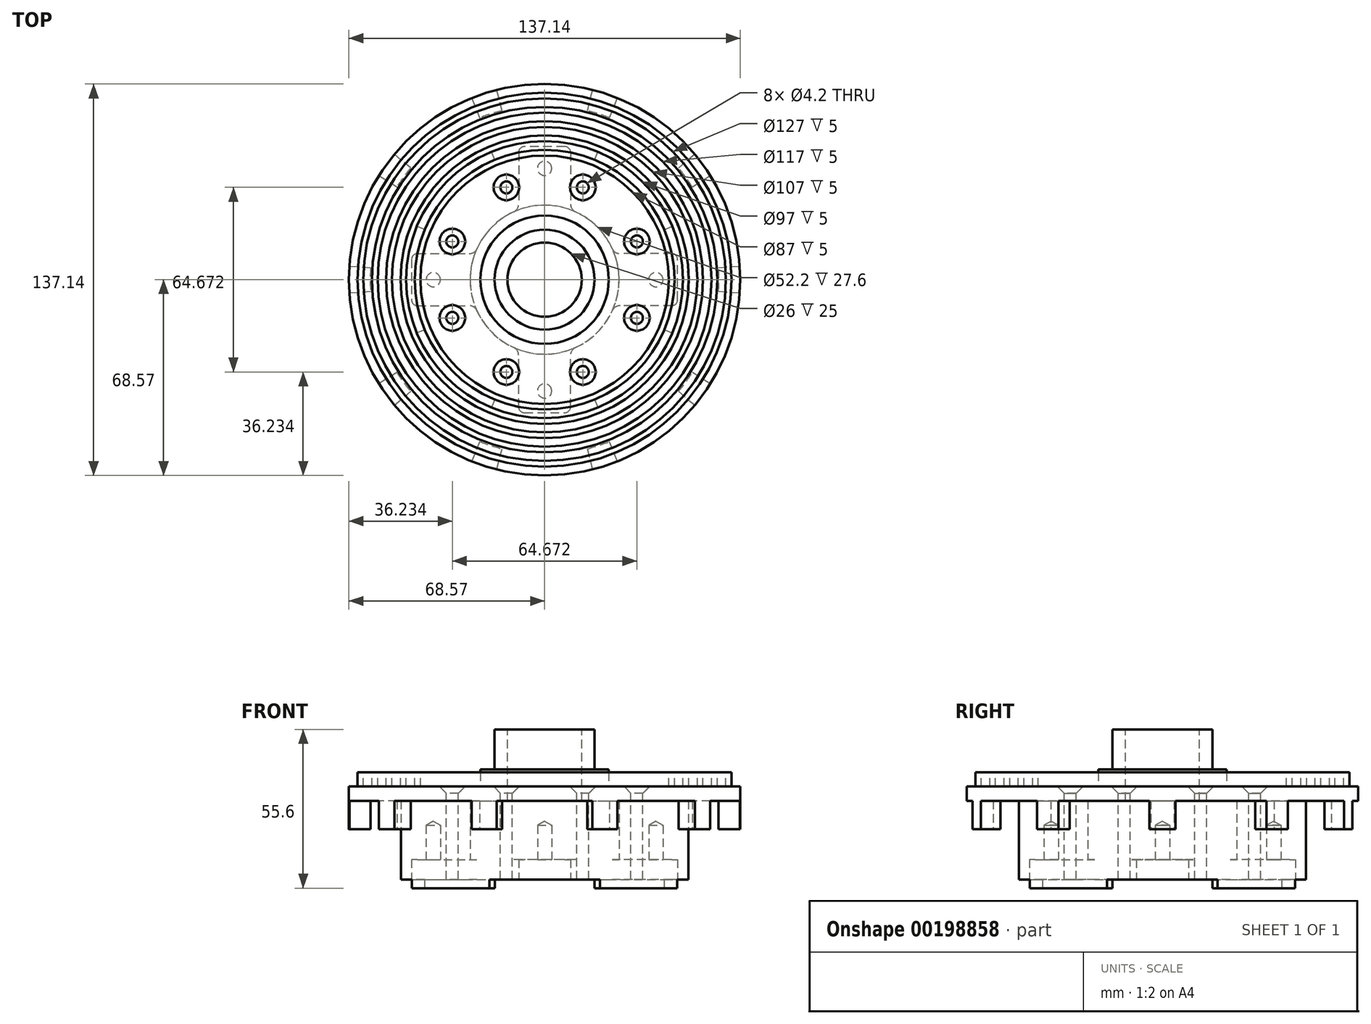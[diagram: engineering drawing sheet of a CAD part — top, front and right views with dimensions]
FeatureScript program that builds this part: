
annotation { "Feature Type Name" : "Feature", "Feature Type Description" : "" }
export const myFeature = defineFeature(function(context is Context, id is Id, definition is map)
    precondition{}
    {
        {
            var Q0;
            Q0=qCreatedBy(makeId("Top.planeOp"),FACE);
            var sketch = newSketch(context, id + "F0", { "sketchPlane" : qUnion([Q0])});
            skCircle(sketch, "E0", {"center": v(0, 0) * mm, "radius": 50.15 * mm, "construction": true});
            skCircle(sketch, "E1", {"center": v(0, 0) * mm, "radius": 68.57 * mm});
            skCircle(sketch, "E2", {"center": v(0, 0) * mm, "radius": 61.01 * mm, "construction": true});
            skSolve(sketch);
        }
        {
            var Q0;
            Q0 = qSketchRegion(id + "F0", true);
            extrude(context, id + "F1", {"entities" : qUnion([Q0]), "depth" : 27.6 * mm});
        }
        {
            var Q0;
            Q0=makeQuery(id+"F1.opExtrude","CAP_FACE",FACE,{"disambiguationData":[OSD([sQuery(id+"F0.wireOp",EDGE,"E1")])],"isStart":true});
            var sketch = newSketch(context, id + "F2", { "sketchPlane" : qUnion([Q0])});
            skLineSegment(sketch, "E3", {"start": v(0, 0) * mm, "end": v(-16.76, -66.49) * mm, "construction": true});
            skLineSegment(sketch, "E4", {"start": v(0, 0) * mm, "end": v(20.02, -79.4) * mm, "construction": true});
            skLineSegment(sketch, "E5", {"start": v(-14.91, -59.15) * mm, "end": v(14.91, -59.15) * mm});
            skLineSegment(sketch, "E6", {"start": v(-14.91, -59.15) * mm, "end": v(-18.58, -73.7) * mm});
            skLineSegment(sketch, "E7", {"start": v(-18.58, -73.7) * mm, "end": v(18.58, -73.7) * mm});
            skLineSegment(sketch, "E8", {"start": v(18.58, -73.7) * mm, "end": v(14.91, -59.15) * mm});
            skSolve(sketch);
        }
        {
            var Q0;
            Q0 = qSketchRegion(id + "F2", true);
            extrude(context, id + "F3", {"entities" : qUnion([Q0]), "endBound" : BoundingType.SYMMETRIC, "depth" : 75 * mm});
        }
        {
            var Q0;
            Q0=makeQuery(id+"F3.opExtrude","SWEPT_BODY",BODY,{"disambiguationData":[OSD([sQuery(id+"F2.wireOp",EDGE,"E5"),sQuery(id+"F2.wireOp",EDGE,"E6"),sQuery(id+"F2.wireOp",EDGE,"E7"),sQuery(id+"F2.wireOp",EDGE,"E8")])]});
            var Q1;
            Q1=makeQuery(id+"F1.opExtrude","SWEPT_FACE",FACE,{"disambiguationData":[OSD([sQuery(id+"F0.wireOp",EDGE,"E1")])]});
            circularPattern(context, id + "F4", {"entities" : qUnion([Q0]), "axis" : qUnion([Q1]), "angle" : 36 * degree, "instanceCount" : 10});
        }
        {
            var Q0;
            Q0=makeQuery(id+"F4.opPattern","COPY",BODY,{"derivedFrom":makeQuery(id+"F3.opExtrude","SWEPT_BODY",BODY,{"disambiguationData":[OSD([sQuery(id+"F2.wireOp",EDGE,"E5"),sQuery(id+"F2.wireOp",EDGE,"E6"),sQuery(id+"F2.wireOp",EDGE,"E7"),sQuery(id+"F2.wireOp",EDGE,"E8")])]}),"instanceName":"7"});
            var Q1;
            Q1=makeQuery(id+"F4.opPattern","COPY",BODY,{"derivedFrom":makeQuery(id+"F3.opExtrude","SWEPT_BODY",BODY,{"disambiguationData":[OSD([sQuery(id+"F2.wireOp",EDGE,"E5"),sQuery(id+"F2.wireOp",EDGE,"E6"),sQuery(id+"F2.wireOp",EDGE,"E7"),sQuery(id+"F2.wireOp",EDGE,"E8")])]}),"instanceName":"8"});
            var Q2;
            Q2=makeQuery(id+"F4.opPattern","COPY",BODY,{"derivedFrom":makeQuery(id+"F3.opExtrude","SWEPT_BODY",BODY,{"disambiguationData":[OSD([sQuery(id+"F2.wireOp",EDGE,"E5"),sQuery(id+"F2.wireOp",EDGE,"E6"),sQuery(id+"F2.wireOp",EDGE,"E7"),sQuery(id+"F2.wireOp",EDGE,"E8")])]}),"instanceName":"9"});
            var Q3;
            Q3=makeQuery(id+"F3.opExtrude","SWEPT_BODY",BODY,{"disambiguationData":[OSD([sQuery(id+"F2.wireOp",EDGE,"E5"),sQuery(id+"F2.wireOp",EDGE,"E6"),sQuery(id+"F2.wireOp",EDGE,"E7"),sQuery(id+"F2.wireOp",EDGE,"E8")])]});
            var Q4;
            Q4=makeQuery(id+"F4.opPattern","COPY",BODY,{"derivedFrom":makeQuery(id+"F3.opExtrude","SWEPT_BODY",BODY,{"disambiguationData":[OSD([sQuery(id+"F2.wireOp",EDGE,"E5"),sQuery(id+"F2.wireOp",EDGE,"E6"),sQuery(id+"F2.wireOp",EDGE,"E7"),sQuery(id+"F2.wireOp",EDGE,"E8")])]}),"instanceName":"1"});
            var Q5;
            Q5=makeQuery(id+"F4.opPattern","COPY",BODY,{"derivedFrom":makeQuery(id+"F3.opExtrude","SWEPT_BODY",BODY,{"disambiguationData":[OSD([sQuery(id+"F2.wireOp",EDGE,"E5"),sQuery(id+"F2.wireOp",EDGE,"E6"),sQuery(id+"F2.wireOp",EDGE,"E7"),sQuery(id+"F2.wireOp",EDGE,"E8")])]}),"instanceName":"2"});
            var Q6;
            Q6=makeQuery(id+"F4.opPattern","COPY",BODY,{"derivedFrom":makeQuery(id+"F3.opExtrude","SWEPT_BODY",BODY,{"disambiguationData":[OSD([sQuery(id+"F2.wireOp",EDGE,"E5"),sQuery(id+"F2.wireOp",EDGE,"E6"),sQuery(id+"F2.wireOp",EDGE,"E7"),sQuery(id+"F2.wireOp",EDGE,"E8")])]}),"instanceName":"3"});
            var Q7;
            Q7=makeQuery(id+"F4.opPattern","COPY",BODY,{"derivedFrom":makeQuery(id+"F3.opExtrude","SWEPT_BODY",BODY,{"disambiguationData":[OSD([sQuery(id+"F2.wireOp",EDGE,"E5"),sQuery(id+"F2.wireOp",EDGE,"E6"),sQuery(id+"F2.wireOp",EDGE,"E7"),sQuery(id+"F2.wireOp",EDGE,"E8")])]}),"instanceName":"4"});
            var Q8;
            Q8=makeQuery(id+"F4.opPattern","COPY",BODY,{"derivedFrom":makeQuery(id+"F3.opExtrude","SWEPT_BODY",BODY,{"disambiguationData":[OSD([sQuery(id+"F2.wireOp",EDGE,"E5"),sQuery(id+"F2.wireOp",EDGE,"E6"),sQuery(id+"F2.wireOp",EDGE,"E7"),sQuery(id+"F2.wireOp",EDGE,"E8")])]}),"instanceName":"5"});
            var Q9;
            Q9=makeQuery(id+"F4.opPattern","COPY",BODY,{"derivedFrom":makeQuery(id+"F3.opExtrude","SWEPT_BODY",BODY,{"disambiguationData":[OSD([sQuery(id+"F2.wireOp",EDGE,"E5"),sQuery(id+"F2.wireOp",EDGE,"E6"),sQuery(id+"F2.wireOp",EDGE,"E7"),sQuery(id+"F2.wireOp",EDGE,"E8")])]}),"instanceName":"6"});
            var Q10;
            Q10=makeQuery(id+"F1.opExtrude","SWEPT_BODY",BODY,{"disambiguationData":[OSD([sQuery(id+"F0.wireOp",EDGE,"E1")])]});
            booleanBodies(context, id + "F5", {"operationType" : BooleanOperationType.SUBTRACTION, "tools" : qUnion([Q0, Q1, Q2, Q3, Q4, Q5, Q6, Q7, Q8, Q9]), "targets" : qUnion([Q10])});
        }
        {
            var Q0;
            Q0=makeQuery(id+"F1.opExtrude","CAP_FACE",FACE,{"disambiguationData":[OSD([sQuery(id+"F0.wireOp",EDGE,"E1")])],"isStart":false});
            var sketch = newSketch(context, id + "F6", { "sketchPlane" : qUnion([Q0])});
            skCircle(sketch, "E9", {"center": v(0, 0) * mm, "radius": 68.57 * mm});
            skSolve(sketch);
        }
        {
            var Q0;
            Q0 = qSketchRegion(id + "F6", true);
            extrude(context, id + "F7", {"entities" : qUnion([Q0]), "operationType" : NewBodyOperationType.ADD, "depth" : 10 * mm});
        }
        {
            var Q0;
            Q0=makeQuery(id+"F1.opExtrude","CAP_FACE",FACE,{"disambiguationData":[OSD([sQuery(id+"F0.wireOp",EDGE,"E1")])],"isStart":true});
            var sketch = newSketch(context, id + "F8", { "sketchPlane" : qUnion([Q0])});
            skCircle(sketch, "E10", {"center": v(0, 0) * mm, "radius": 50.35 * mm});
            skCircle(sketch, "E11", {"center": v(0, 0) * mm, "radius": 61.1 * mm});
            skSolve(sketch);
        }
        {
            var Q0;
            Q0 = qSketchRegion(id + "F8", true);
            extrude(context, id + "F9", {"entities" : qUnion([Q0]), "operationType" : NewBodyOperationType.REMOVE, "oppositeDirection" : true, "depth" : 27.6 * mm});
        }
        {
            var Q0;
            Q0=qCreatedBy(makeId("Front.planeOp"),FACE);
            var sketch = newSketch(context, id + "F10", { "sketchPlane" : qUnion([Q0])});
            skLineSegment(sketch, "E12", {"start": v(0, 42.6) * mm, "end": v(-100, 42.6) * mm});
            skLineSegment(sketch, "E13", {"start": v(-100, 42.6) * mm, "end": v(-100, 32.6) * mm});
            skLineSegment(sketch, "E14", {"start": v(-100, 32.6) * mm, "end": v(-65.5, 32.6) * mm});
            skLineSegment(sketch, "E15", {"start": v(-65.5, 32.6) * mm, "end": v(-65.5, 39.6) * mm});
            skLineSegment(sketch, "E16", {"start": v(-65.5, 39.6) * mm, "end": v(-63.5, 39.6) * mm});
            skLineSegment(sketch, "E17", {"start": v(-63.5, 39.6) * mm, "end": v(-63.5, 32.6) * mm});
            skLineSegment(sketch, "E18", {"start": v(-63.5, 32.6) * mm, "end": v(-60.5, 32.6) * mm});
            skLineSegment(sketch, "E19", {"start": v(-60.5, 32.6) * mm, "end": v(-60.5, 39.6) * mm});
            skLineSegment(sketch, "E20", {"start": v(-60.5, 39.6) * mm, "end": v(-58.5, 39.6) * mm});
            skLineSegment(sketch, "E21", {"start": v(-58.5, 39.6) * mm, "end": v(-58.5, 32.6) * mm});
            skLineSegment(sketch, "E22", {"start": v(-58.5, 32.6) * mm, "end": v(-55.5, 32.6) * mm});
            skLineSegment(sketch, "E23", {"start": v(-55.5, 32.6) * mm, "end": v(-55.5, 39.6) * mm});
            skLineSegment(sketch, "E24", {"start": v(-55.5, 39.6) * mm, "end": v(-53.5, 39.6) * mm});
            skLineSegment(sketch, "E25", {"start": v(-53.5, 39.6) * mm, "end": v(-53.5, 32.6) * mm});
            skLineSegment(sketch, "E26", {"start": v(-53.5, 32.6) * mm, "end": v(-50.5, 32.6) * mm});
            skLineSegment(sketch, "E27", {"start": v(-50.5, 32.6) * mm, "end": v(-50.5, 39.6) * mm});
            skLineSegment(sketch, "E28", {"start": v(-50.5, 39.6) * mm, "end": v(-48.5, 39.6) * mm});
            skLineSegment(sketch, "E29", {"start": v(-48.5, 39.6) * mm, "end": v(-48.5, 32.6) * mm});
            skLineSegment(sketch, "E30", {"start": v(-48.5, 32.6) * mm, "end": v(-45.5, 32.6) * mm});
            skLineSegment(sketch, "E31", {"start": v(-45.5, 32.6) * mm, "end": v(-45.5, 39.6) * mm});
            skLineSegment(sketch, "E32", {"start": v(-45.5, 39.6) * mm, "end": v(-43.5, 39.6) * mm});
            skLineSegment(sketch, "E33", {"start": v(-43.5, 39.6) * mm, "end": v(-43.5, 32.6) * mm});
            skLineSegment(sketch, "E34", {"start": v(-43.5, 32.6) * mm, "end": v(0, 32.6) * mm});
            skLineSegment(sketch, "E35", {"start": v(0, 32.6) * mm, "end": v(0, 42.6) * mm});
            skSolve(sketch);
        }
        {
            var Q0;
            Q0 = qSketchRegion(id + "F10", true);
            var Q1;
            Q1=sQuery(id+"F10.wireOp",EDGE,"E35");
            revolve(context, id + "F11", {"operationType" : NewBodyOperationType.REMOVE, "entities" : qUnion([Q0]), "axis" : qUnion([Q1]), "revolveType" : RevolveType.FULL, "oppositeDirection" : true});
        }
        {
            var Q0;
            Q0=makeQuery(id+"F11.boolean.opBoolean","COPY",FACE,{"derivedFrom":makeQuery(id+"F11.opRevolve","SWEPT_FACE",FACE,{"disambiguationData":[OSD([sQuery(id+"F10.wireOp",EDGE,"E34")])]})});
            var sketch = newSketch(context, id + "F12", { "sketchPlane" : qUnion([Q0])});
            skCircle(sketch, "E36", {"center": v(0, 0) * mm, "radius": 22.5 * mm});
            skSolve(sketch);
        }
        {
            var Q0;
            Q0 = qSketchRegion(id + "F12", true);
            extrude(context, id + "F13", {"entities" : qUnion([Q0]), "operationType" : NewBodyOperationType.ADD, "depth" : 6 * mm});
        }
        {
            var Q0;
            Q0=makeQuery(id+"F13.opExtrude","CAP_FACE",FACE,{"disambiguationData":[OSD([sQuery(id+"F12.wireOp",EDGE,"E36")])],"isStart":false});
            var sketch = newSketch(context, id + "F14", { "sketchPlane" : qUnion([Q0])});
            skCircle(sketch, "E37", {"center": v(0, 0) * mm, "radius": 17.5 * mm});
            skSolve(sketch);
        }
        {
            var Q0;
            Q0 = qSketchRegion(id + "F14", true);
            extrude(context, id + "F15", {"entities" : qUnion([Q0]), "operationType" : NewBodyOperationType.ADD, "depth" : 14 * mm});
        }
        {
            var Q0;
            Q0=makeQuery(id+"F9.boolean.opBoolean","SPLIT",FACE,{"disambiguationData":[TD([makeQuery(id+"F9.opExtrude","SWEPT_FACE",FACE,{"disambiguationData":[OSD([sQuery(id+"F8.wireOp",EDGE,"E10")])]})])],"derivedFrom":makeQuery(id+"F1.opExtrude","CAP_FACE",FACE,{"disambiguationData":[OSD([sQuery(id+"F0.wireOp",EDGE,"E1")])],"isStart":true})});
            var sketch = newSketch(context, id + "F16", { "sketchPlane" : qUnion([Q0])});
            skCircle(sketch, "E38", {"center": v(0, 0) * mm, "radius": 55 * mm});
            skCircle(sketch, "E39", {"center": v(0, 0) * mm, "radius": 90 * mm});
            skSolve(sketch);
        }
        {
            var Q0;
            Q0 = qSketchRegion(id + "F16", true);
            extrude(context, id + "F17", {"entities" : qUnion([Q0]), "operationType" : NewBodyOperationType.REMOVE, "oppositeDirection" : true, "depth" : 17.6 * mm});
        }
        {
            var Q0;
            Q0=makeQuery(id+"F9.boolean.opBoolean","SPLIT",FACE,{"disambiguationData":[TD([makeQuery(id+"F9.opExtrude","SWEPT_FACE",FACE,{"disambiguationData":[OSD([sQuery(id+"F8.wireOp",EDGE,"E10")])]})])],"derivedFrom":makeQuery(id+"F1.opExtrude","CAP_FACE",FACE,{"disambiguationData":[OSD([sQuery(id+"F0.wireOp",EDGE,"E1")])],"isStart":true})});
            var sketch = newSketch(context, id + "F18", { "sketchPlane" : qUnion([Q0])});
            skCircle(sketch, "E40", {"center": v(0, 0) * mm, "radius": 26.1 * mm});
            skSolve(sketch);
        }
        {
            var Q0;
            Q0 = qSketchRegion(id + "F18", true);
            extrude(context, id + "F19", {"entities" : qUnion([Q0]), "operationType" : NewBodyOperationType.REMOVE, "oppositeDirection" : true, "depth" : 27.6 * mm});
        }
        {
            var Q0;
            Q0=makeQuery(id+"F9.boolean.opBoolean","SPLIT",FACE,{"disambiguationData":[TD([makeQuery(id+"F9.opExtrude","SWEPT_FACE",FACE,{"disambiguationData":[OSD([sQuery(id+"F8.wireOp",EDGE,"E10")])]})])],"derivedFrom":makeQuery(id+"F1.opExtrude","CAP_FACE",FACE,{"disambiguationData":[OSD([sQuery(id+"F0.wireOp",EDGE,"E1")])],"isStart":true})});
            var sketch = newSketch(context, id + "F20", { "sketchPlane" : qUnion([Q0])});
            skLineSegment(sketch, "E41", {"start": v(0, 0) * mm, "end": v(42.3, 0) * mm, "construction": true});
            skLineSegment(sketch, "E42", {"start": v(46.6, 0) * mm, "end": v(46.6, -7.1) * mm});
            skLineSegment(sketch, "E43", {"start": v(44.6, -9.1) * mm, "end": v(26.47, -9.1) * mm});
            skLineSegment(sketch, "E44", {"start": v(0, 0) * mm, "end": v(28.28, -28.28) * mm, "construction": true});
            skLineSegment(sketch, "E45.MirrorCS", {"start": v(9.1, -44.6) * mm, "end": v(9.1, -26.47) * mm});
            skLineSegment(sketch, "E46.MirrorCS", {"start": v(0, -46.6) * mm, "end": v(7.1, -46.6) * mm});
            skArc(sketch, "E47", {"start": v(23.74, -10.85) * mm, "mid": v(18.46, -18.46) * mm, "end": v(10.85, -23.74) * mm});
            skPoint(sketch, "E48.visualSharp", {"position": v(46.6, -9.1) * mm});
            skArc(sketch, "E48.filletArc", {"start": v(44.6, -9.1) * mm, "mid": v(46.01, -8.51) * mm, "end": v(46.6, -7.1) * mm});
            skPoint(sketch, "E49.visualSharp", {"position": v(9.1, -46.6) * mm});
            skArc(sketch, "E49.filletArc", {"start": v(7.1, -46.6) * mm, "mid": v(8.51, -46.01) * mm, "end": v(9.1, -44.6) * mm});
            skPoint(sketch, "E50.visualSharp", {"position": v(24.46, -9.1) * mm});
            skArc(sketch, "E50.filletArc", {"start": v(26.47, -9.1) * mm, "mid": v(24.84, -9.58) * mm, "end": v(23.74, -10.85) * mm});
            skPoint(sketch, "E51.visualSharp", {"position": v(9.1, -24.46) * mm});
            skArc(sketch, "E51.filletArc", {"start": v(10.85, -23.74) * mm, "mid": v(9.58, -24.84) * mm, "end": v(9.1, -26.47) * mm});
            skLineSegment(sketch, "E52.MirrorCS", {"start": v(46.6, 0) * mm, "end": v(46.6, 7.1) * mm});
            skArc(sketch, "E53.MirrorCS", {"start": v(44.6, 9.1) * mm, "mid": v(46.01, 8.51) * mm, "end": v(46.6, 7.1) * mm});
            skLineSegment(sketch, "E54.MirrorCS", {"start": v(44.6, 9.1) * mm, "end": v(26.47, 9.1) * mm});
            skArc(sketch, "E55.MirrorCS", {"start": v(26.47, 9.1) * mm, "mid": v(24.84, 9.58) * mm, "end": v(23.74, 10.85) * mm});
            skArc(sketch, "E56.MirrorCS", {"start": v(23.74, 10.85) * mm, "mid": v(18.46, 18.46) * mm, "end": v(10.85, 23.74) * mm});
            skArc(sketch, "E57.MirrorCS", {"start": v(10.85, 23.74) * mm, "mid": v(9.58, 24.84) * mm, "end": v(9.1, 26.47) * mm});
            skLineSegment(sketch, "E58.MirrorCS", {"start": v(9.1, 44.6) * mm, "end": v(9.1, 26.47) * mm});
            skArc(sketch, "E59.MirrorCS", {"start": v(7.1, 46.6) * mm, "mid": v(8.51, 46.01) * mm, "end": v(9.1, 44.6) * mm});
            skLineSegment(sketch, "E60.MirrorCS", {"start": v(0, 46.6) * mm, "end": v(7.1, 46.6) * mm});
            skLineSegment(sketch, "E61", {"start": v(0, 0) * mm, "end": v(0, -19.41) * mm, "construction": true});
            skLineSegment(sketch, "E62.MirrorCS", {"start": v(0, 46.6) * mm, "end": v(-7.1, 46.6) * mm});
            skArc(sketch, "E63.MirrorCS", {"start": v(-7.1, 46.6) * mm, "mid": v(-8.51, 46.01) * mm, "end": v(-9.1, 44.6) * mm});
            skLineSegment(sketch, "E64.MirrorCS", {"start": v(-9.1, 44.6) * mm, "end": v(-9.1, 26.47) * mm});
            skArc(sketch, "E65.MirrorCS", {"start": v(-10.85, 23.74) * mm, "mid": v(-9.58, 24.84) * mm, "end": v(-9.1, 26.47) * mm});
            skArc(sketch, "E66.MirrorCS", {"start": v(-23.74, 10.85) * mm, "mid": v(-18.46, 18.46) * mm, "end": v(-10.85, 23.74) * mm});
            skArc(sketch, "E67.MirrorCS", {"start": v(-26.47, 9.1) * mm, "mid": v(-24.84, 9.58) * mm, "end": v(-23.74, 10.85) * mm});
            skLineSegment(sketch, "E68.MirrorCS", {"start": v(-44.6, 9.1) * mm, "end": v(-26.47, 9.1) * mm});
            skArc(sketch, "E69.MirrorCS", {"start": v(-44.6, 9.1) * mm, "mid": v(-46.01, 8.51) * mm, "end": v(-46.6, 7.1) * mm});
            skLineSegment(sketch, "E70.MirrorCS", {"start": v(-46.6, 0) * mm, "end": v(-46.6, 7.1) * mm});
            skLineSegment(sketch, "E71.MirrorCS", {"start": v(-46.6, 0) * mm, "end": v(-46.6, -7.1) * mm});
            skArc(sketch, "E72.MirrorCS", {"start": v(-44.6, -9.1) * mm, "mid": v(-46.01, -8.51) * mm, "end": v(-46.6, -7.1) * mm});
            skLineSegment(sketch, "E73.MirrorCS", {"start": v(-44.6, -9.1) * mm, "end": v(-26.47, -9.1) * mm});
            skArc(sketch, "E74.MirrorCS", {"start": v(-26.47, -9.1) * mm, "mid": v(-24.84, -9.58) * mm, "end": v(-23.74, -10.85) * mm});
            skArc(sketch, "E75.MirrorCS", {"start": v(-23.74, -10.85) * mm, "mid": v(-18.46, -18.46) * mm, "end": v(-10.85, -23.74) * mm});
            skArc(sketch, "E76.MirrorCS", {"start": v(-10.85, -23.74) * mm, "mid": v(-9.58, -24.84) * mm, "end": v(-9.1, -26.47) * mm});
            skLineSegment(sketch, "E77.MirrorCS", {"start": v(-9.1, -44.6) * mm, "end": v(-9.1, -26.47) * mm});
            skArc(sketch, "E78.MirrorCS", {"start": v(-7.1, -46.6) * mm, "mid": v(-8.51, -46.01) * mm, "end": v(-9.1, -44.6) * mm});
            skLineSegment(sketch, "E79.MirrorCS", {"start": v(0, -46.6) * mm, "end": v(-7.1, -46.6) * mm});
            skSolve(sketch);
        }
        {
            var Q0;
            Q0 = qSketchRegion(id + "F20", true);
            extrude(context, id + "F21", {"entities" : qUnion([Q0]), "operationType" : NewBodyOperationType.REMOVE, "oppositeDirection" : true, "depth" : 7 * mm});
        }
        {
            var Q0;
            {var subQ0=sQuery(id+"F20.wireOp",EDGE,"E58.MirrorCS");var subQ1=sQuery(id+"F20.wireOp",EDGE,"E57.MirrorCS");var subQ2=sQuery(id+"F20.wireOp",EDGE,"E59.MirrorCS");var subQ3=sQuery(id+"F20.wireOp",EDGE,"E62.MirrorCS");var subQ4=sQuery(id+"F20.wireOp",EDGE,"E60.MirrorCS");var subQ5=sQuery(id+"F20.wireOp",EDGE,"E63.MirrorCS");var subQ6=sQuery(id+"F20.wireOp",EDGE,"E64.MirrorCS");var subQ7=sQuery(id+"F20.wireOp",EDGE,"E65.MirrorCS");Q0=makeQuery(id+"F21.boolean.opBoolean","COPY",FACE,{"disambiguationData":[TD([makeQuery(id+"F21.opExtrude","SWEPT_FACE",FACE,{"disambiguationData":[OSD([subQ1])]})])],"derivedFrom":makeQuery(id+"F21.opExtrude","CAP_FACE",FACE,{"disambiguationData":[OSD([sQuery(id+"F20.wireOp",EDGE,"E42"),sQuery(id+"F20.wireOp",EDGE,"E43"),sQuery(id+"F20.wireOp",EDGE,"E45.MirrorCS"),sQuery(id+"F20.wireOp",EDGE,"E46.MirrorCS"),sQuery(id+"F20.wireOp",EDGE,"E47"),sQuery(id+"F20.wireOp",EDGE,"E48.filletArc"),sQuery(id+"F20.wireOp",EDGE,"E49.filletArc"),sQuery(id+"F20.wireOp",EDGE,"E50.filletArc"),sQuery(id+"F20.wireOp",EDGE,"E51.filletArc"),sQuery(id+"F20.wireOp",EDGE,"E52.MirrorCS"),sQuery(id+"F20.wireOp",EDGE,"E53.MirrorCS"),sQuery(id+"F20.wireOp",EDGE,"E54.MirrorCS"),sQuery(id+"F20.wireOp",EDGE,"E55.MirrorCS"),sQuery(id+"F20.wireOp",EDGE,"E56.MirrorCS"),subQ1,subQ0,subQ2,subQ4,subQ3,subQ5,subQ6,subQ7,sQuery(id+"F20.wireOp",EDGE,"E66.MirrorCS"),sQuery(id+"F20.wireOp",EDGE,"E67.MirrorCS"),sQuery(id+"F20.wireOp",EDGE,"E68.MirrorCS"),sQuery(id+"F20.wireOp",EDGE,"E69.MirrorCS"),sQuery(id+"F20.wireOp",EDGE,"E70.MirrorCS"),sQuery(id+"F20.wireOp",EDGE,"E71.MirrorCS"),sQuery(id+"F20.wireOp",EDGE,"E72.MirrorCS"),sQuery(id+"F20.wireOp",EDGE,"E73.MirrorCS"),sQuery(id+"F20.wireOp",EDGE,"E74.MirrorCS"),sQuery(id+"F20.wireOp",EDGE,"E75.MirrorCS"),sQuery(id+"F20.wireOp",EDGE,"E76.MirrorCS"),sQuery(id+"F20.wireOp",EDGE,"E77.MirrorCS"),sQuery(id+"F20.wireOp",EDGE,"E78.MirrorCS"),sQuery(id+"F20.wireOp",EDGE,"E79.MirrorCS")])],"isStart":false})});}
            var sketch = newSketch(context, id + "F22", { "sketchPlane" : qUnion([Q0])});
            skCircle(sketch, "E80", {"center": v(0, 0) * mm, "radius": 39 * mm, "construction": true});
            skPoint(sketch, "E81", {"position": v(39, 0) * mm});
            skPoint(sketch, "E82", {"position": v(0, -39) * mm});
            skPoint(sketch, "E83", {"position": v(-39, 0) * mm});
            skPoint(sketch, "E84", {"position": v(0, 39) * mm});
            skSolve(sketch);
        }
        {
            var Q0;
            Q0=sQuery(id+"F22.wireOp",VERTEX,"E81");
            var Q1;
            Q1=sQuery(id+"F22.wireOp",VERTEX,"E82");
            var Q2;
            Q2=sQuery(id+"F22.wireOp",VERTEX,"E83");
            var Q3;
            Q3=sQuery(id+"F22.wireOp",VERTEX,"E84");
            var Q4;
            Q4=makeQuery(id+"F1.opExtrude","SWEPT_BODY",BODY,{"disambiguationData":[OSD([sQuery(id+"F0.wireOp",EDGE,"E1")])]});
            hole(context, id + "F23", {"style" : HoleStyle.SIMPLE, "endStyle" : HoleEndStyle.BLIND, "standardTappedOrClearance" : lookupTablePath({ "standard" : "ISO", "engagement" : "75%", "pitch" : "1 mm", "size" : "M6", "type" : "Tapped" }), "standardBlindInLast" : lookupTablePath({ "standard" : "ISO", "engagement" : "75%", "pitch" : "1 mm", "size" : "M6", "type" : "Tapped" }), "holeDiameter" : 5 * mm, "holeDepth" : 12 * mm, "locations" : qUnion([Q0, Q1, Q2, Q3]), "scope" : qUnion([Q4]), "majorDiameter" : 6 * mm});
        }
        {
            var Q0;
            Q0=makeQuery(id+"F11.boolean.opBoolean","COPY",FACE,{"derivedFrom":makeQuery(id+"F11.opRevolve","SWEPT_FACE",FACE,{"disambiguationData":[OSD([sQuery(id+"F10.wireOp",EDGE,"E34")])]})});
            var sketch = newSketch(context, id + "F24", { "sketchPlane" : qUnion([Q0])});
            skLineSegment(sketch, "E85", {"start": v(0, 0) * mm, "end": v(-16.96, -40.95) * mm, "construction": true});
            skPoint(sketch, "E86", {"position": v(-13.4, -32.34) * mm});
            skPoint(sketch, "E87.1.0", {"position": v(13.4, -32.34) * mm});
            skPoint(sketch, "E87.2.0", {"position": v(32.34, -13.4) * mm});
            skPoint(sketch, "E87.3.0", {"position": v(32.34, 13.4) * mm});
            skPoint(sketch, "E87.4.0", {"position": v(13.4, 32.34) * mm});
            skPoint(sketch, "E87.5.0", {"position": v(-13.4, 32.34) * mm});
            skPoint(sketch, "E87.6.0", {"position": v(-32.34, 13.4) * mm});
            skPoint(sketch, "E87.7.0", {"position": v(-32.34, -13.4) * mm});
            skPoint(sketch, "E87.center", {"position": v(0, 0) * mm});
            skSolve(sketch);
        }
        {
            var Q0;
            Q0=sQuery(id+"F24.wireOp",VERTEX,"E86");
            var Q1;
            Q1=sQuery(id+"F24.wireOp",VERTEX,"E87.1.0");
            var Q2;
            Q2=sQuery(id+"F24.wireOp",VERTEX,"E87.2.0");
            var Q3;
            Q3=sQuery(id+"F24.wireOp",VERTEX,"E87.3.0");
            var Q4;
            Q4=sQuery(id+"F24.wireOp",VERTEX,"E87.4.0");
            var Q5;
            Q5=sQuery(id+"F24.wireOp",VERTEX,"E87.5.0");
            var Q6;
            Q6=sQuery(id+"F24.wireOp",VERTEX,"E87.6.0");
            var Q7;
            Q7=sQuery(id+"F24.wireOp",VERTEX,"E87.7.0");
            var Q8;
            Q8=makeQuery(id+"F1.opExtrude","SWEPT_BODY",BODY,{"disambiguationData":[OSD([sQuery(id+"F0.wireOp",EDGE,"E1")])]});
            hole(context, id + "F25", {"style" : HoleStyle.C_SINK, "endStyle" : HoleEndStyle.THROUGH, "standardTappedOrClearance" : lookupTablePath({ "standard" : "ISO", "fit" : "Close", "size" : "M4", "type" : "Clearance" }), "standardBlindInLast" : lookupTablePath({ "fit" : "Close", "standard" : "ISO", "size" : "M4", "type" : "Clearance" }), "holeDiameter" : 4.2 * mm, "cSinkDiameter" : 8.96 * mm, "cSinkAngle" : 90 * degree, "locations" : qUnion([Q0, Q1, Q2, Q3, Q4, Q5, Q6, Q7]), "scope" : qUnion([Q8]), "isTappedThrough" : true});
        }
        {
            var Q0;
            Q0=makeQuery(id+"F15.opExtrude","CAP_FACE",FACE,{"disambiguationData":[OSD([sQuery(id+"F14.wireOp",EDGE,"E37")])],"isStart":false});
            var sketch = newSketch(context, id + "F26", { "sketchPlane" : qUnion([Q0])});
            skCircle(sketch, "E88", {"center": v(0, 0) * mm, "radius": 13 * mm});
            skSolve(sketch);
        }
        {
            var Q0;
            Q0 = qSketchRegion(id + "F26", true);
            extrude(context, id + "F27", {"entities" : qUnion([Q0]), "operationType" : NewBodyOperationType.REMOVE, "endBound" : BoundingType.THROUGH_ALL, "oppositeDirection" : true, "depth" : 25 * mm});
        }
        {
            var Q0;
            Q0=makeQuery(id+"F9.boolean.opBoolean","SPLIT",FACE,{"disambiguationData":[TD([makeQuery(id+"F9.opExtrude","SWEPT_FACE",FACE,{"disambiguationData":[OSD([sQuery(id+"F8.wireOp",EDGE,"E10")])]})])],"derivedFrom":makeQuery(id+"F1.opExtrude","CAP_FACE",FACE,{"disambiguationData":[OSD([sQuery(id+"F0.wireOp",EDGE,"E1")])],"isStart":true})});
            var sketch = newSketch(context, id + "F28", { "sketchPlane" : qUnion([Q0])});
            skLineSegment(sketch, "E89", {"start": v(0, 0) * mm, "end": v(37.55, 37.55) * mm, "construction": true});
            skLineSegment(sketch, "E90", {"start": v(0, 0) * mm, "end": v(56.18, 23.27) * mm, "construction": true});
            skLineSegment(sketch, "E91", {"start": v(41.95, 17.49) * mm, "end": v(46.48, 19.36) * mm});
            skArc(sketch, "E92", {"start": v(41.95, 17.49) * mm, "mid": v(37.76, 25.3) * mm, "end": v(32.14, 32.14) * mm});
            skArc(sketch, "E93", {"start": v(46.48, 19.36) * mm, "mid": v(41.84, 28.01) * mm, "end": v(35.6, 35.6) * mm});
            skArc(sketch, "E94.MirrorCS", {"start": v(19.36, 46.48) * mm, "mid": v(28.01, 41.84) * mm, "end": v(35.6, 35.6) * mm});
            skLineSegment(sketch, "E95.MirrorCS", {"start": v(17.49, 41.95) * mm, "end": v(19.36, 46.48) * mm});
            skArc(sketch, "E96.MirrorCS", {"start": v(17.49, 41.95) * mm, "mid": v(25.3, 37.76) * mm, "end": v(32.14, 32.14) * mm});
            skLineSegment(sketch, "E97.MirrorCS", {"start": v(-17.49, 41.95) * mm, "end": v(-19.36, 46.48) * mm});
            skArc(sketch, "E98.MirrorCS", {"start": v(-19.36, 46.48) * mm, "mid": v(-28.01, 41.84) * mm, "end": v(-35.6, 35.6) * mm});
            skArc(sketch, "E99.MirrorCS", {"start": v(-46.48, 19.36) * mm, "mid": v(-41.84, 28.01) * mm, "end": v(-35.6, 35.6) * mm});
            skLineSegment(sketch, "E100.MirrorCS", {"start": v(-41.95, 17.49) * mm, "end": v(-46.48, 19.36) * mm});
            skArc(sketch, "E101.MirrorCS", {"start": v(-41.95, 17.49) * mm, "mid": v(-37.76, 25.3) * mm, "end": v(-32.14, 32.14) * mm});
            skArc(sketch, "E102.MirrorCS", {"start": v(-17.49, 41.95) * mm, "mid": v(-25.3, 37.76) * mm, "end": v(-32.14, 32.14) * mm});
            skLineSegment(sketch, "E103.MirrorCS", {"start": v(41.95, -17.49) * mm, "end": v(46.48, -19.36) * mm});
            skArc(sketch, "E104.MirrorCS", {"start": v(41.95, -17.49) * mm, "mid": v(37.76, -25.3) * mm, "end": v(32.14, -32.14) * mm});
            skArc(sketch, "E105.MirrorCS", {"start": v(17.49, -41.95) * mm, "mid": v(25.3, -37.76) * mm, "end": v(32.14, -32.14) * mm});
            skLineSegment(sketch, "E106.MirrorCS", {"start": v(17.49, -41.95) * mm, "end": v(19.36, -46.48) * mm});
            skArc(sketch, "E107.MirrorCS", {"start": v(19.36, -46.48) * mm, "mid": v(28.01, -41.84) * mm, "end": v(35.6, -35.6) * mm});
            skArc(sketch, "E108.MirrorCS", {"start": v(46.48, -19.36) * mm, "mid": v(41.84, -28.01) * mm, "end": v(35.6, -35.6) * mm});
            skArc(sketch, "E109.MirrorCS", {"start": v(-17.49, -41.95) * mm, "mid": v(-25.3, -37.76) * mm, "end": v(-32.14, -32.14) * mm});
            skArc(sketch, "E110.MirrorCS", {"start": v(-41.95, -17.49) * mm, "mid": v(-37.76, -25.3) * mm, "end": v(-32.14, -32.14) * mm});
            skLineSegment(sketch, "E111.MirrorCS", {"start": v(-41.95, -17.49) * mm, "end": v(-46.48, -19.36) * mm});
            skArc(sketch, "E112.MirrorCS", {"start": v(-46.48, -19.36) * mm, "mid": v(-41.84, -28.01) * mm, "end": v(-35.6, -35.6) * mm});
            skArc(sketch, "E113.MirrorCS", {"start": v(-19.36, -46.48) * mm, "mid": v(-28.01, -41.84) * mm, "end": v(-35.6, -35.6) * mm});
            skLineSegment(sketch, "E114.MirrorCS", {"start": v(-17.49, -41.95) * mm, "end": v(-19.36, -46.48) * mm});
            skSolve(sketch);
        }
        {
            var Q0;
            Q0 = qSketchRegion(id + "F28", true);
            extrude(context, id + "F29", {"entities" : qUnion([Q0]), "operationType" : NewBodyOperationType.ADD, "depth" : 3 * mm});
        }
    });
